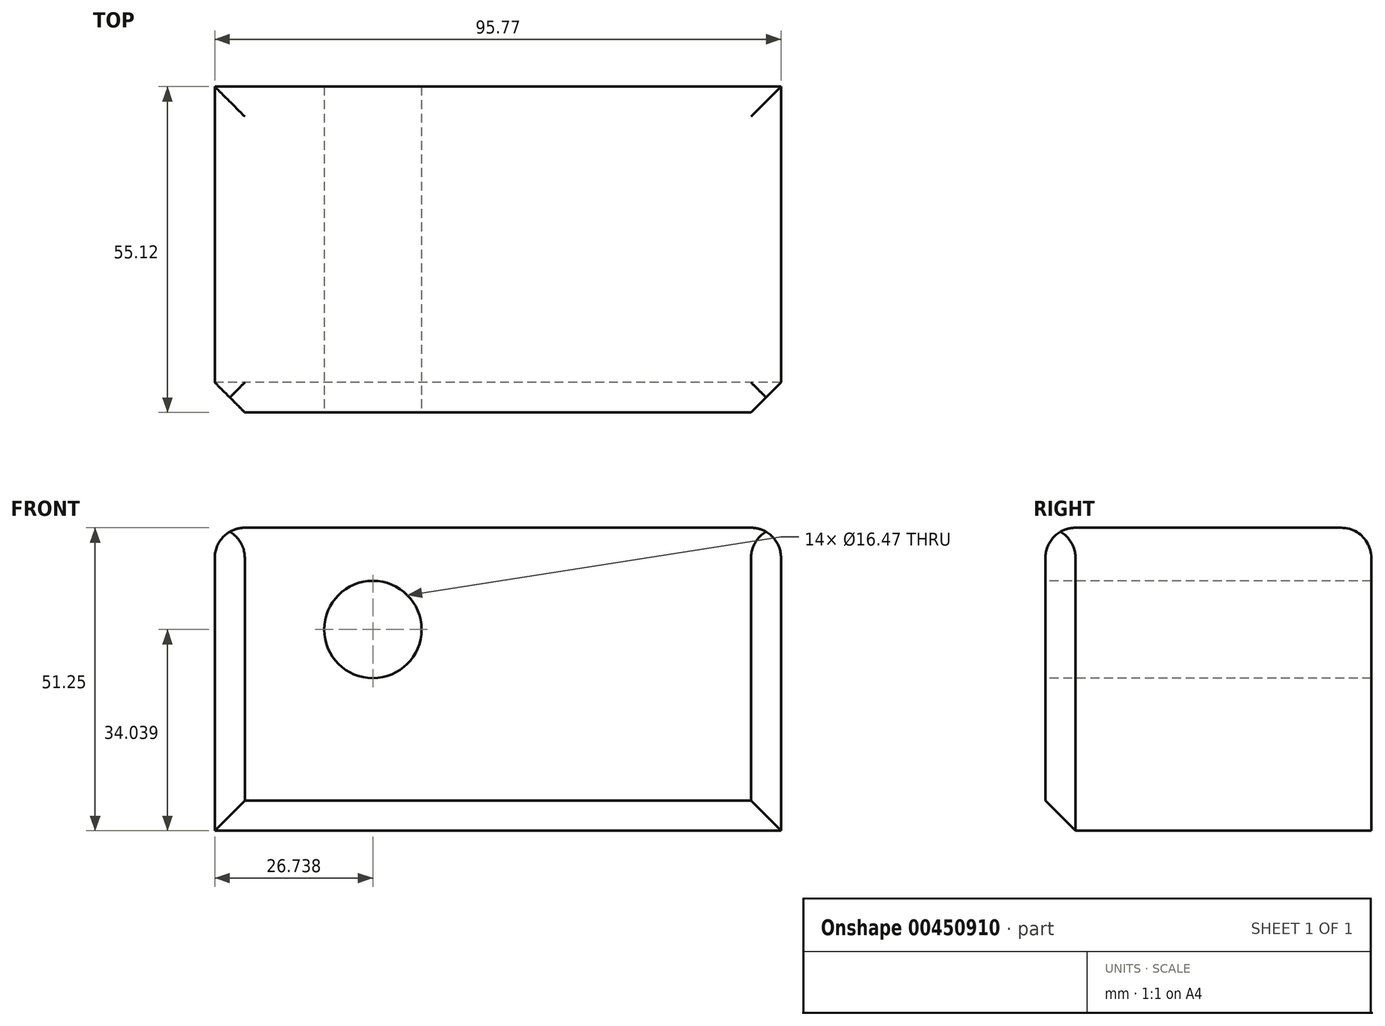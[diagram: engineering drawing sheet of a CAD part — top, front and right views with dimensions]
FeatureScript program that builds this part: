
annotation { "Feature Type Name" : "Feature", "Feature Type Description" : "" }
export const myFeature = defineFeature(function(context is Context, id is Id, definition is map)
    precondition{}
    {
        {
            var Q0;
            Q0=qCreatedBy(makeId("Front.planeOp"),FACE);
            var sketch = newSketch(context, id + "F0", { "sketchPlane" : qUnion([Q0])});
            skLineSegment(sketch, "E0.bottom", {"start": v(-68.21, 31.35) * mm, "end": v(27.56, 31.35) * mm});
            skLineSegment(sketch, "E0.top", {"start": v(-68.21, -19.9) * mm, "end": v(27.56, -19.9) * mm});
            skLineSegment(sketch, "E0.left", {"start": v(-68.21, 31.35) * mm, "end": v(-68.21, -19.9) * mm});
            skLineSegment(sketch, "E0.right", {"start": v(27.56, 31.35) * mm, "end": v(27.56, -19.9) * mm});
            skSolve(sketch);
        }
        {
            var Q0;
            Q0=makeQuery(id+"F0.imprint","IMPRINT",FACE,{"disambiguationData":[TD([[makeQuery(id+"F0.imprint","IMPRINT",EDGE,{"derivedFrom":sQuery(id+"F0.wireOp",EDGE,"E0.bottom")}),-1.0]])]});
            extrude(context, id + "F1", {"entities" : qUnion([Q0]), "depth" : 55.12 * mm});
        }
        {
            var Q0;
            Q0=makeQuery(id+"F1.opExtrude","SWEPT_FACE",FACE,{"disambiguationData":[OSD([sQuery(id+"F0.wireOp",EDGE,"E0.bottom")])]});
            fillet(context, id + "F2", {"entities" : qUnion([Q0]), "radius" : 5.08 * mm, "tangentPropagation" : true, "allowEdgeOverflow" : false});
        }
        {
            var Q0;
            Q0=makeQuery(id+"F1.opExtrude","CAP_FACE",FACE,{"disambiguationData":[OSD([sQuery(id+"F0.wireOp",EDGE,"E0.bottom"),sQuery(id+"F0.wireOp",EDGE,"E0.top"),sQuery(id+"F0.wireOp",EDGE,"E0.left"),sQuery(id+"F0.wireOp",EDGE,"E0.right")])],"isStart":false});
            chamfer(context, id + "F3", {"entities" : qUnion([Q0]), "width" : 5.08 * mm, "tangentPropagation" : true});
        }
        {
            var Q0;
            Q0=makeQuery(id+"F1.opExtrude","CAP_FACE",FACE,{"disambiguationData":[OSD([sQuery(id+"F0.wireOp",EDGE,"E0.bottom"),sQuery(id+"F0.wireOp",EDGE,"E0.top"),sQuery(id+"F0.wireOp",EDGE,"E0.left"),sQuery(id+"F0.wireOp",EDGE,"E0.right")])],"isStart":false});
            var sketch = newSketch(context, id + "F4", { "sketchPlane" : qUnion([Q0])});
            skCircle(sketch, "E1", {"center": v(-41.47, 14.14) * mm, "radius": 8.24 * mm});
            skSolve(sketch);
        }
        {
            var Q0;
            Q0 = qSketchRegion(id + "F4", true);
            extrude(context, id + "F5", {"entities" : qUnion([Q0]), "operationType" : NewBodyOperationType.REMOVE, "oppositeDirection" : true, "depth" : 129.03 * mm});
        }
    });
